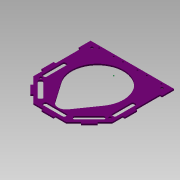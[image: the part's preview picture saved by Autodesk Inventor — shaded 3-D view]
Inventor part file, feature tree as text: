
AUTODESK INVENTOR PART (.ipt)
format: ipt  version: 2015 SP1 (Build 190203100, 203)  size: 410,112 bytes
history: native  units: mm
features: sketch x9, extrude x7, plane x1
ambient origin geometry x8: Origin, YZ Plane, XZ Plane, XY Plane, X Axis, Y Axis, Z Axis, Center Point
bodies: Body1 (feature_tree)
feature tree (17):
  sketch  "Sketch1"  dims[d10=3.0mm d11=3.0mm]
  plane  "Work Plane2"
  sketch  "Sketch2"  dims[d12=135.0deg d14=3.0mm]
  extrude  "Extrusion4"  Depth=3.0mm
  extrude  "Extrusion5"  Depth=3.0mm
  extrude  "Extrusion6"  Depth=3.0mm
  sketch  "Sketch4"  dims[d17=3.0mm d18=3.0mm]
  extrude  "Extrusion7"  Depth=3.0mm
  sketch  "Sketch6"  dims[d24=2.0mm d25=2.0mm]
  extrude  "Extrusion9"  Depth=3.0mm TaperAngle=0.0deg
  extrude  "Extrusion10"  Depth=2.0mm
  extrude  "Extrusion11"  Depth=2.0mm
  sketch  "Sketch3"  dims[d15=3.0mm d16=3.0mm]
  sketch  "Sketch5"  dims[d19=2.0mm d20=0.0mm d21=3.0mm d22=0.0mm]
  sketch  "Sketch8"  dims[d26=2.0mm d27=2.0mm]
  sketch  "Sketch9"  dims[d28=6.0mm]
  sketch  "Sketch10"  dims[d29=6.0mm d30=21.0mm d31=21.0mm d32=3.0mm d33=12.5mm d35=12.5mm d36=2.0mm d37=2.0mm d38=2.0mm d39=21.0mm d40=21.0mm d41=10.5mm d42=10.5mm d43=10.0mm d44=0.0mm d45=10.0mm d46=0.0mm d54=5.0mm d68=2.0mm d71=2.0mm d72=10.0mm d73=0.0mm d74=6.0mm d76=6.0mm d77=6.0mm d78=6.0mm d79=6.0mm d80=4.353mm d82=10.0mm d83=0.0mm d84=0.558116mm d85=2.0mm d86=0.0mm]
